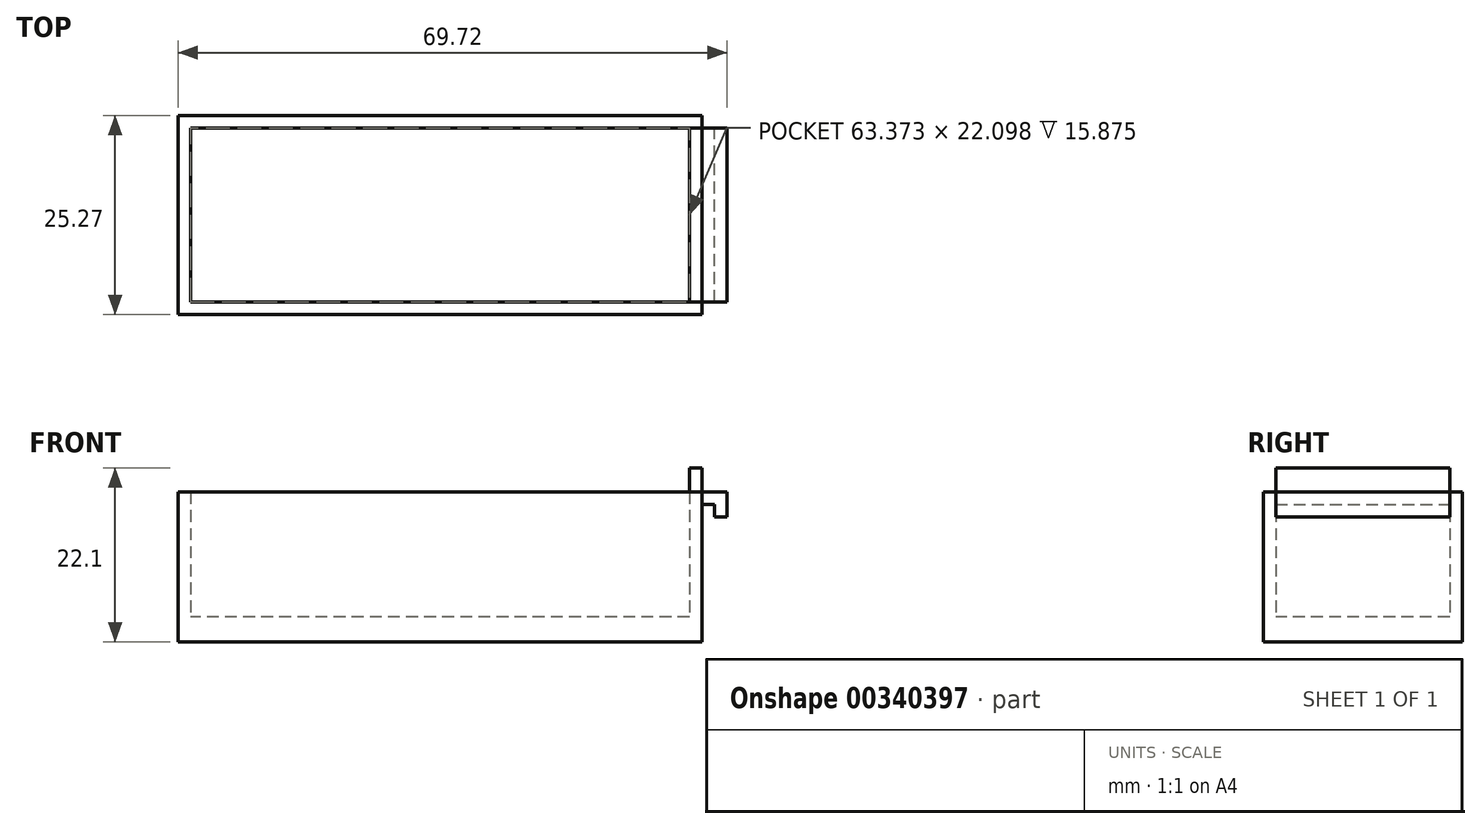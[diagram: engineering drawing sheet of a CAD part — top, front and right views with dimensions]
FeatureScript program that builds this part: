
annotation { "Feature Type Name" : "Feature", "Feature Type Description" : "" }
export const myFeature = defineFeature(function(context is Context, id is Id, definition is map)
    precondition{}
    {
        {
            var Q0;
            Q0=qCreatedBy(makeId("Top.planeOp"),FACE);
            var sketch = newSketch(context, id + "F0", { "sketchPlane" : qUnion([Q0])});
            skLineSegment(sketch, "E0.bottom", {"start": v(0, 0) * mm, "end": v(66.55, 0) * mm});
            skLineSegment(sketch, "E0.top", {"start": v(0, -25.27) * mm, "end": v(66.55, -25.27) * mm});
            skLineSegment(sketch, "E0.left", {"start": v(0, 0) * mm, "end": v(0, -25.27) * mm});
            skLineSegment(sketch, "E0.right", {"start": v(66.55, 0) * mm, "end": v(66.55, -25.27) * mm});
            skSolve(sketch);
        }
        {
            var Q0;
            Q0=makeQuery(id+"F0.imprint","IMPRINT",FACE,{"disambiguationData":[TD([[makeQuery(id+"F0.imprint","IMPRINT",EDGE,{"derivedFrom":sQuery(id+"F0.wireOp",EDGE,"E0.bottom")}),-1.0]])]});
            extrude(context, id + "F1", {"entities" : qUnion([Q0]), "depth" : 3.17 * mm});
        }
        {
            var Q0;
            Q0=makeQuery(id+"F1.opExtrude","CAP_FACE",FACE,{"disambiguationData":[OSD([sQuery(id+"F0.wireOp",EDGE,"E0.bottom"),sQuery(id+"F0.wireOp",EDGE,"E0.top"),sQuery(id+"F0.wireOp",EDGE,"E0.left"),sQuery(id+"F0.wireOp",EDGE,"E0.right")])],"isStart":false});
            var sketch = newSketch(context, id + "F2", { "sketchPlane" : qUnion([Q0])});
            skLineSegment(sketch, "E1.0", {"start": v(1.59, -1.59) * mm, "end": v(1.59, -23.69) * mm});
            skLineSegment(sketch, "E1.1", {"start": v(64.96, -1.59) * mm, "end": v(1.59, -1.59) * mm});
            skLineSegment(sketch, "E1.2", {"start": v(64.96, -23.69) * mm, "end": v(64.96, -1.59) * mm});
            skLineSegment(sketch, "E1.3", {"start": v(1.59, -23.69) * mm, "end": v(64.96, -23.69) * mm});
            skSolve(sketch);
        }
        {
            var Q0;
            Q0=makeQuery(id+"F2.imprint","IMPRINT",FACE,{"disambiguationData":[TD([[makeQuery(id+"F2.imprint","IMPRINT",EDGE,{"derivedFrom":sQuery(id+"F2.wireOp",EDGE,"E1.0")}),-1.0]])]});
            extrude(context, id + "F3", {"entities" : qUnion([Q0]), "operationType" : NewBodyOperationType.ADD, "depth" : 15.88 * mm});
        }
        {
            var Q0;
            Q0=makeQuery(id+"F3.opExtrude","CAP_FACE",FACE,{"disambiguationData":[OSD([sQuery(id+"F0.wireOp",EDGE,"E0.bottom"),sQuery(id+"F0.wireOp",EDGE,"E0.top"),sQuery(id+"F0.wireOp",EDGE,"E0.left"),sQuery(id+"F0.wireOp",EDGE,"E0.right"),sQuery(id+"F2.wireOp",EDGE,"E1.0"),sQuery(id+"F2.wireOp",EDGE,"E1.1"),sQuery(id+"F2.wireOp",EDGE,"E1.2"),sQuery(id+"F2.wireOp",EDGE,"E1.3")])],"isStart":false});
            var sketch = newSketch(context, id + "F4", { "sketchPlane" : qUnion([Q0])});
            skLineSegment(sketch, "E2", {"start": v(64.96, -23.69) * mm, "end": v(66.55, -23.69) * mm});
            skLineSegment(sketch, "E3", {"start": v(64.96, -1.59) * mm, "end": v(66.55, -1.59) * mm});
            skSolve(sketch);
        }
        {
            var Q0;
            {var subQ0=sQuery(id+"F4.wireOp",EDGE,"E2");Q0=makeQuery(id+"F4.imprint","IMPRINT",FACE,{"disambiguationData":[TD([[makeQuery(id+"F4.imprint","IMPRINT",EDGE,{"derivedFrom":subQ0}),1.0]])]});}
            extrude(context, id + "F5", {"entities" : qUnion([Q0]), "operationType" : NewBodyOperationType.ADD, "depth" : 3.05 * mm});
        }
        {
            var Q0;
            {var subQ0=sQuery(id+"F0.wireOp",EDGE,"E0.right");Q0=makeQuery(id+"F5.boolean.opBoolean","MERGE",FACE,{"derivedFrom":[makeQuery(id+"F3.boolean.opBoolean","MERGE",FACE,{"derivedFrom":[makeQuery(id+"F1.opExtrude","SWEPT_FACE",FACE,{"disambiguationData":[OSD([subQ0])]}),makeQuery(id+"F3.opExtrude","SWEPT_FACE",FACE,{"disambiguationData":[OSD([subQ0])]})]}),makeQuery(id+"F5.opExtrude","SWEPT_FACE",FACE,{"disambiguationData":[OSD([subQ0])]})]});}
            var sketch = newSketch(context, id + "F6", { "sketchPlane" : qUnion([Q0])});
            skLineSegment(sketch, "E4.bottom", {"start": v(-23.69, 19.05) * mm, "end": v(-1.59, 19.05) * mm});
            skLineSegment(sketch, "E4.top", {"start": v(-23.69, 17.46) * mm, "end": v(-1.59, 17.46) * mm});
            skLineSegment(sketch, "E4.left", {"start": v(-23.69, 19.05) * mm, "end": v(-23.69, 17.46) * mm});
            skLineSegment(sketch, "E4.right", {"start": v(-1.59, 19.05) * mm, "end": v(-1.59, 17.46) * mm});
            skSolve(sketch);
        }
        {
            var Q0;
            Q0=makeQuery(id+"F6.imprint","IMPRINT",FACE,{"disambiguationData":[TD([[makeQuery(id+"F6.imprint","IMPRINT",EDGE,{"derivedFrom":sQuery(id+"F6.wireOp",EDGE,"E4.bottom")}),-1.0]])]});
            extrude(context, id + "F7", {"entities" : qUnion([Q0]), "operationType" : NewBodyOperationType.ADD, "depth" : 3.17 * mm});
        }
        {
            var Q0;
            Q0=makeQuery(id+"F7.opExtrude","SWEPT_FACE",FACE,{"disambiguationData":[OSD([sQuery(id+"F6.wireOp",EDGE,"E4.top")])]});
            var sketch = newSketch(context, id + "F8", { "sketchPlane" : qUnion([Q0])});
            skLineSegment(sketch, "E5.bottom", {"start": v(69.72, 23.69) * mm, "end": v(68.14, 23.69) * mm});
            skLineSegment(sketch, "E5.top", {"start": v(69.72, 1.59) * mm, "end": v(68.14, 1.59) * mm});
            skLineSegment(sketch, "E5.left", {"start": v(69.72, 23.69) * mm, "end": v(69.72, 1.59) * mm});
            skLineSegment(sketch, "E5.right", {"start": v(68.14, 23.69) * mm, "end": v(68.14, 1.59) * mm});
            skSolve(sketch);
        }
        {
            var Q0;
            Q0=makeQuery(id+"F8.imprint","IMPRINT",FACE,{"disambiguationData":[TD([[makeQuery(id+"F8.imprint","IMPRINT",EDGE,{"derivedFrom":sQuery(id+"F8.wireOp",EDGE,"E5.bottom")}),1.0]])]});
            extrude(context, id + "F9", {"entities" : qUnion([Q0]), "operationType" : NewBodyOperationType.ADD, "depth" : 1.59 * mm});
        }
    });
